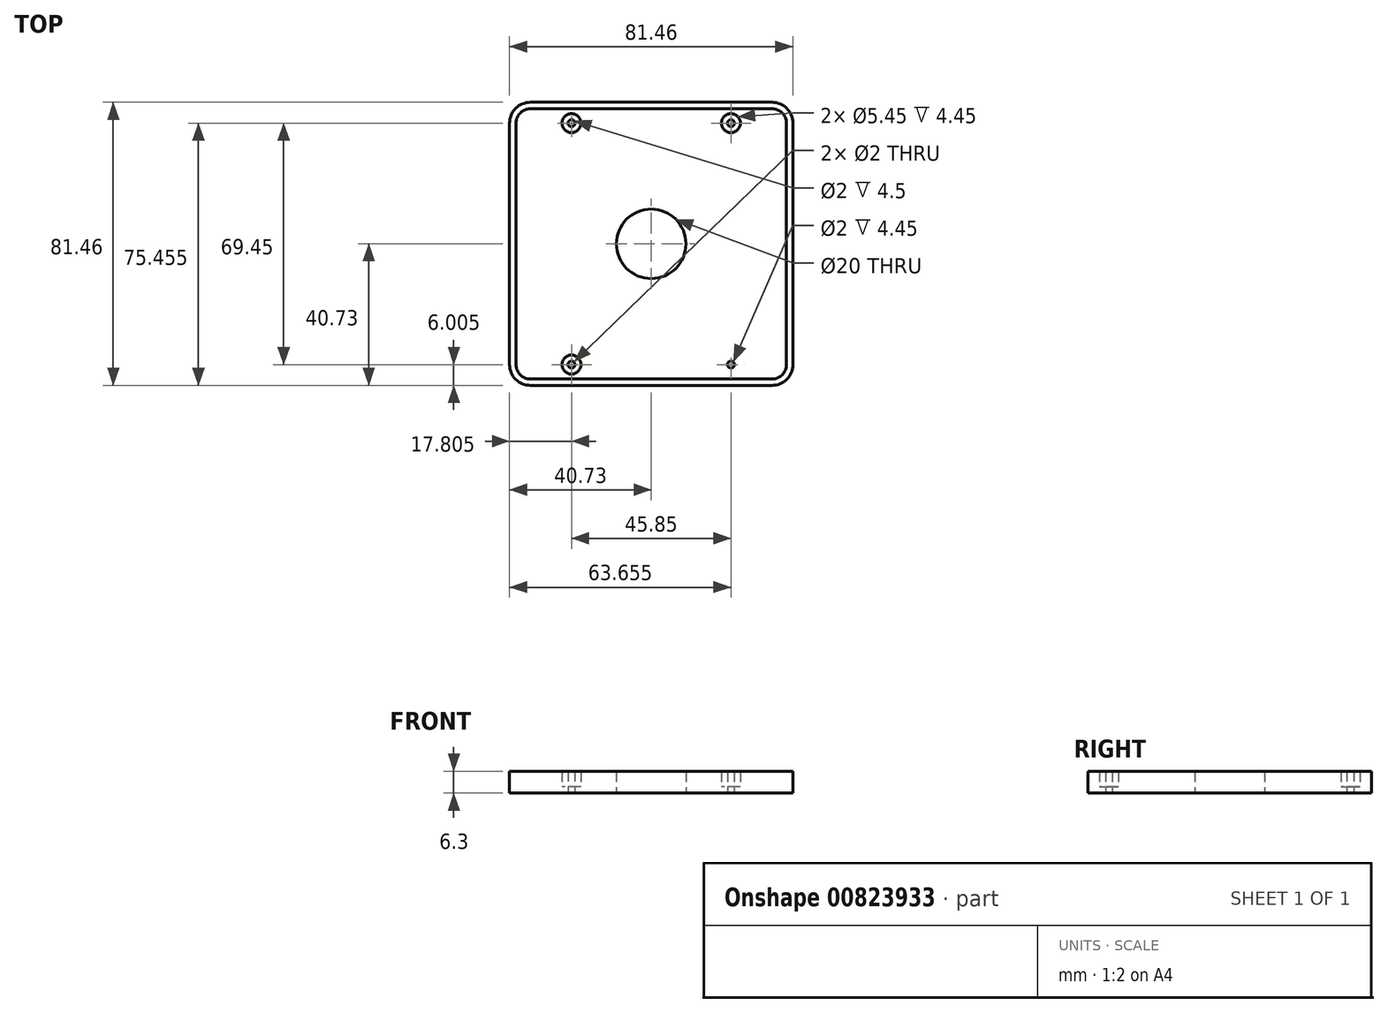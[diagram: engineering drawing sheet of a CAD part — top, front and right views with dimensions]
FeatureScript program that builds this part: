
annotation { "Feature Type Name" : "Feature", "Feature Type Description" : "" }
export const myFeature = defineFeature(function(context is Context, id is Id, definition is map)
    precondition{}
    {
        {
            var Q0;
            Q0=qCreatedBy(makeId("Top.planeOp"),FACE);
            var sketch = newSketch(context, id + "F0", { "sketchPlane" : qUnion([Q0])});
            skLineSegment(sketch, "E0.bottom", {"start": v(34.73, -40.72) * mm, "end": v(-34.73, -40.72) * mm});
            skLineSegment(sketch, "E0.top", {"start": v(34.73, 40.73) * mm, "end": v(-34.73, 40.73) * mm});
            skLineSegment(sketch, "E0.left", {"start": v(40.72, -34.72) * mm, "end": v(40.72, 34.73) * mm});
            skLineSegment(sketch, "E0.right", {"start": v(-40.72, -34.73) * mm, "end": v(-40.72, 34.73) * mm});
            skPoint(sketch, "E0.middle", {"position": v(0, 0) * mm});
            skPoint(sketch, "E1.visualSharp", {"position": v(-40.72, 40.73) * mm});
            skArc(sketch, "E1.filletArc", {"start": v(-34.73, 40.73) * mm, "mid": v(-38.97, 38.97) * mm, "end": v(-40.72, 34.73) * mm});
            skPoint(sketch, "E2.visualSharp", {"position": v(-40.72, -40.72) * mm});
            skArc(sketch, "E2.filletArc", {"start": v(-40.72, -34.73) * mm, "mid": v(-38.97, -38.97) * mm, "end": v(-34.73, -40.72) * mm});
            skPoint(sketch, "E3.visualSharp", {"position": v(40.73, 40.73) * mm});
            skArc(sketch, "E3.filletArc", {"start": v(40.73, 34.73) * mm, "mid": v(38.97, 38.97) * mm, "end": v(34.73, 40.73) * mm});
            skPoint(sketch, "E4.visualSharp", {"position": v(40.72, -40.72) * mm});
            skArc(sketch, "E4.filletArc", {"start": v(34.73, -40.72) * mm, "mid": v(38.97, -38.97) * mm, "end": v(40.72, -34.72) * mm});
            skLineSegment(sketch, "E5", {"start": v(-22.93, 40.73) * mm, "end": v(-22.93, 34.73) * mm, "construction": true});
            skCircle(sketch, "E6", {"center": v(-22.93, 34.73) * mm, "radius": 2.73 * mm});
            skCircle(sketch, "E7", {"center": v(-22.93, 34.73) * mm, "radius": 1 * mm});
            skArc(sketch, "E8.0", {"start": v(38.88, 34.73) * mm, "mid": v(37.66, 37.66) * mm, "end": v(34.73, 38.88) * mm});
            skLineSegment(sketch, "E8.1", {"start": v(38.88, -34.72) * mm, "end": v(38.88, 34.73) * mm});
            skLineSegment(sketch, "E8.2", {"start": v(34.73, 38.88) * mm, "end": v(-34.73, 38.88) * mm});
            skArc(sketch, "E8.3", {"start": v(34.73, -38.88) * mm, "mid": v(37.66, -37.66) * mm, "end": v(38.88, -34.72) * mm});
            skArc(sketch, "E8.4", {"start": v(-34.73, 38.88) * mm, "mid": v(-37.66, 37.66) * mm, "end": v(-38.88, 34.73) * mm});
            skLineSegment(sketch, "E8.5", {"start": v(-38.87, -34.73) * mm, "end": v(-38.88, 34.73) * mm});
            skArc(sketch, "E8.6", {"start": v(-38.88, -34.73) * mm, "mid": v(-37.66, -37.66) * mm, "end": v(-34.72, -38.88) * mm});
            skLineSegment(sketch, "E8.7", {"start": v(34.73, -38.87) * mm, "end": v(-34.72, -38.88) * mm});
            skCircle(sketch, "E9.MirrorC", {"center": v(22.93, 34.73) * mm, "radius": 2.73 * mm});
            skCircle(sketch, "E10.MirrorC", {"center": v(22.93, 34.73) * mm, "radius": 1 * mm});
            skCircle(sketch, "E11.MirrorC", {"center": v(-22.93, -34.73) * mm, "radius": 2.73 * mm});
            skCircle(sketch, "E12.MirrorC", {"center": v(-22.93, -34.73) * mm, "radius": 1 * mm});
            skCircle(sketch, "E13.MirrorC", {"center": v(22.93, -34.73) * mm, "radius": 2.73 * mm});
            skCircle(sketch, "E14.MirrorC", {"center": v(22.93, -34.73) * mm, "radius": 1 * mm});
            skCircle(sketch, "E15", {"center": v(0, 0) * mm, "radius": 10 * mm});
            skSolve(sketch);
        }
        {
            var Q0;
            Q0=makeQuery(id+"F0.imprint","IMPRINT",FACE,{"disambiguationData":[TD([[makeQuery(id+"F0.imprint","IMPRINT",EDGE,{"derivedFrom":sQuery(id+"F0.wireOp",EDGE,"E6")}),-1.0]])]});
            var Q1;
            Q1=makeQuery(id+"F0.imprint","IMPRINT",FACE,{"disambiguationData":[TD([[makeQuery(id+"F0.imprint","IMPRINT",EDGE,{"derivedFrom":sQuery(id+"F0.wireOp",EDGE,"E6")}),1.0]])]});
            var Q2;
            Q2=makeQuery(id+"F0.imprint","IMPRINT",FACE,{"disambiguationData":[TD([[makeQuery(id+"F0.imprint","IMPRINT",EDGE,{"derivedFrom":sQuery(id+"F0.wireOp",EDGE,"E7")}),1.0]])]});
            var Q3;
            Q3=makeQuery(id+"F0.imprint","IMPRINT",FACE,{"disambiguationData":[TD([[makeQuery(id+"F0.imprint","IMPRINT",EDGE,{"derivedFrom":sQuery(id+"F0.wireOp",EDGE,"E13.MirrorC")}),1.0]])]});
            var Q4;
            Q4=makeQuery(id+"F0.imprint","IMPRINT",FACE,{"disambiguationData":[TD([[makeQuery(id+"F0.imprint","IMPRINT",EDGE,{"derivedFrom":sQuery(id+"F0.wireOp",EDGE,"E14.MirrorC")}),1.0]])]});
            var Q5;
            Q5=makeQuery(id+"F0.imprint","IMPRINT",FACE,{"disambiguationData":[TD([[makeQuery(id+"F0.imprint","IMPRINT",EDGE,{"derivedFrom":sQuery(id+"F0.wireOp",EDGE,"E11.MirrorC")}),-1.0]])]});
            var Q6;
            Q6=makeQuery(id+"F0.imprint","IMPRINT",FACE,{"disambiguationData":[TD([[makeQuery(id+"F0.imprint","IMPRINT",EDGE,{"derivedFrom":sQuery(id+"F0.wireOp",EDGE,"E12.MirrorC")}),-1.0]])]});
            var Q7;
            Q7=makeQuery(id+"F0.imprint","IMPRINT",FACE,{"disambiguationData":[TD([[makeQuery(id+"F0.imprint","IMPRINT",EDGE,{"derivedFrom":sQuery(id+"F0.wireOp",EDGE,"E9.MirrorC")}),-1.0]])]});
            var Q8;
            Q8=makeQuery(id+"F0.imprint","IMPRINT",FACE,{"disambiguationData":[TD([[makeQuery(id+"F0.imprint","IMPRINT",EDGE,{"derivedFrom":sQuery(id+"F0.wireOp",EDGE,"E10.MirrorC")}),-1.0]])]});
            extrude(context, id + "F1", {"entities" : qUnion([Q0, Q1, Q2, Q3, Q4, Q5, Q6, Q7, Q8]), "depth" : 1.8 * mm, "offsetDistance" : 25 * mm});
        }
        {
            var Q0;
            Q0=makeQuery(id+"F0.imprint","IMPRINT",FACE,{"disambiguationData":[TD([[makeQuery(id+"F0.imprint","IMPRINT",EDGE,{"derivedFrom":sQuery(id+"F0.wireOp",EDGE,"E0.bottom")}),-1.0]])]});
            extrude(context, id + "F2", {"entities" : qUnion([Q0]), "operationType" : NewBodyOperationType.ADD, "depth" : 6.3 * mm, "offsetDistance" : 25 * mm});
        }
        {
            var Q0;
            Q0=makeQuery(id+"F0.imprint","IMPRINT",FACE,{"disambiguationData":[TD([[makeQuery(id+"F0.imprint","IMPRINT",EDGE,{"derivedFrom":sQuery(id+"F0.wireOp",EDGE,"E6")}),1.0]])]});
            extrude(context, id + "F3", {"entities" : qUnion([Q0]), "operationType" : NewBodyOperationType.ADD, "depth" : 6.3 * mm, "offsetDistance" : 25 * mm});
        }
        {
            var Q0;
            Q0=makeQuery(id+"F0.imprint","IMPRINT",FACE,{"disambiguationData":[TD([[makeQuery(id+"F0.imprint","IMPRINT",EDGE,{"derivedFrom":sQuery(id+"F0.wireOp",EDGE,"E9.MirrorC")}),-1.0]])]});
            var Q1;
            Q1=makeQuery(id+"F0.imprint","IMPRINT",FACE,{"disambiguationData":[TD([[makeQuery(id+"F0.imprint","IMPRINT",EDGE,{"derivedFrom":sQuery(id+"F0.wireOp",EDGE,"E13.MirrorC")}),1.0]])]});
            var Q2;
            Q2=makeQuery(id+"F0.imprint","IMPRINT",FACE,{"disambiguationData":[TD([[makeQuery(id+"F0.imprint","IMPRINT",EDGE,{"derivedFrom":sQuery(id+"F0.wireOp",EDGE,"E11.MirrorC")}),-1.0]])]});
            extrude(context, id + "F4", {"entities" : qUnion([Q0, Q1, Q2]), "operationType" : NewBodyOperationType.ADD, "depth" : 6.25 * mm, "offsetDistance" : 25 * mm});
        }
    });
